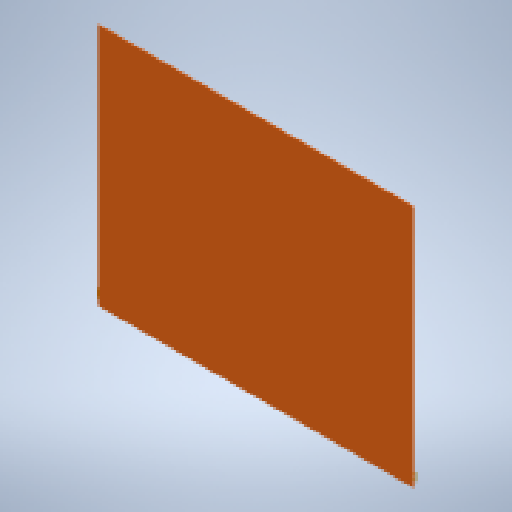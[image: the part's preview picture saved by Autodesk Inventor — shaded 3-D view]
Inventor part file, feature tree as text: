
AUTODESK INVENTOR PART (.ipt)
format: ipt  version: 2025 (Build 290162000, 162)  size: 119,808 bytes
history: native  units: in
note: dims shown in document units (in); Inventor stores cm internally (conversion verified against a paired STEP export)
features: reference x12, other x11, plane x1, extrude x1, sketch x1
ambient origin geometry x8: Origin, YZ Plane, XZ Plane, XY Plane, X Axis, Y Axis, Z Axis, Center Point
bodies: Solid1 (feature_tree)
feature tree (26):
  plane  "Work Plane1"
  extrude  "Extrusion1"  [1 undecoded]
  sketch  "Sketch1"  dims[d0=0.25in d1=0.0in]
  reference  "Reference1"
  reference  "Reference2"
  reference  "Reference3"
  reference  "Reference4"
  reference  "Reference5"
  reference  "Reference6"
  reference  "Reference7"
  reference  "Reference8"
  reference  "Reference9"
  reference  "Reference10"
  reference  "Reference11"
  reference  "Reference12"
  other  "<userpath>\Documents\GitHub\USCTigerBurn24\v2\Tiger.iam"
  other  "Tiger.iam"
  other  "2x4x88:7"
  other  "2x4x120:6"
  other  "2x4x120:4"
  other  "4x4x66:5"
  other  "4x4x96:13"
  other  "4x4x66:4"
  other  "2x4x72:1"
  other  "2x4x72:11"
  other  "2x4x88:3"
note: 1 required parameter value undecoded (feature->parameter linkage not recoverable at this tier; creation-order binding heuristic only, values carry confidence <= 0.55)
